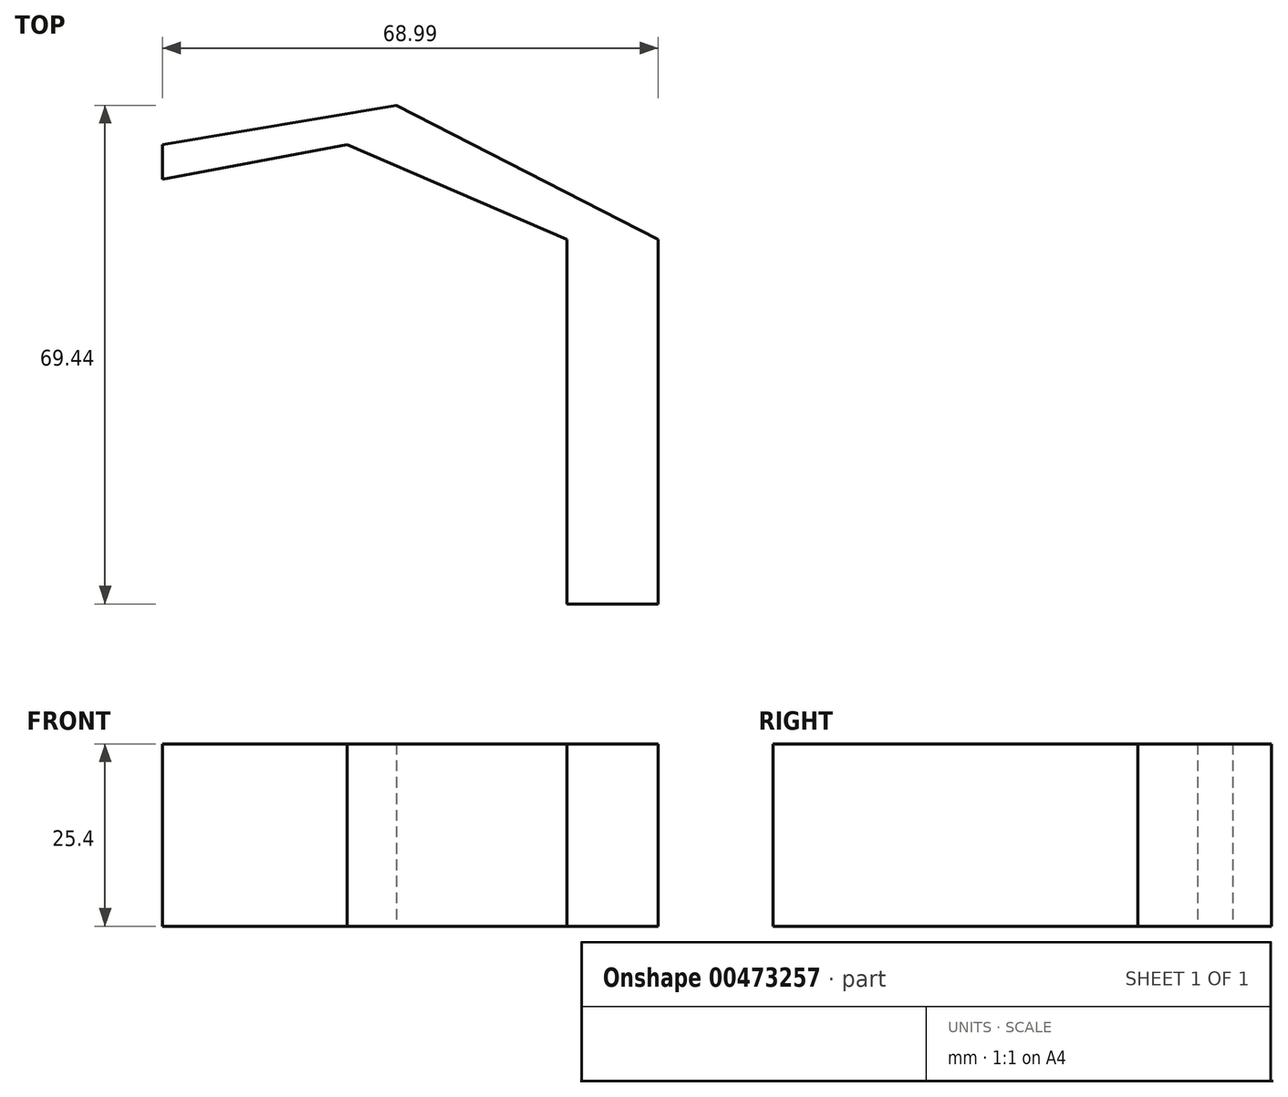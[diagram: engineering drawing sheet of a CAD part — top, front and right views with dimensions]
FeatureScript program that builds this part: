
annotation { "Feature Type Name" : "Feature", "Feature Type Description" : "" }
export const myFeature = defineFeature(function(context is Context, id is Id, definition is map)
    precondition{}
    {
        {
            var Q0;
            Q0=qCreatedBy(makeId("Top.planeOp"),FACE);
            var sketch = newSketch(context, id + "F0", { "sketchPlane" : qUnion([Q0])});
            skLineSegment(sketch, "E0.bottom", {"start": v(0, 0) * mm, "end": v(12.7, 0) * mm});
            skLineSegment(sketch, "E0.top", {"start": v(0, 50.8) * mm, "end": v(12.7, 50.8) * mm});
            skLineSegment(sketch, "E0.left", {"start": v(0, 0) * mm, "end": v(0, 50.8) * mm});
            skLineSegment(sketch, "E0.right", {"start": v(12.7, 0) * mm, "end": v(12.7, 50.8) * mm});
            skLineSegment(sketch, "E1", {"start": v(0, 50.8) * mm, "end": v(-30.58, 64) * mm});
            skLineSegment(sketch, "E2", {"start": v(-23.72, 69.44) * mm, "end": v(12.7, 50.8) * mm});
            skLineSegment(sketch, "E3", {"start": v(-23.72, 69.44) * mm, "end": v(-56.3, 64) * mm});
            skLineSegment(sketch, "E4", {"start": v(-56.3, 59.15) * mm, "end": v(-30.58, 64) * mm});
            skLineSegment(sketch, "E5", {"start": v(-56.3, 64) * mm, "end": v(-56.3, 59.15) * mm});
            skLineSegment(sketch, "E6", {"start": v(-23.72, 69.44) * mm, "end": v(-30.58, 64) * mm});
            skSolve(sketch);
        }
        {
            var Q0;
            Q0 = qSketchRegion(id + "F0", true);
            extrude(context, id + "F1", {"entities" : qUnion([Q0]), "depth" : 25.4 * mm});
        }
    });
